# Revit family: 13323XXX
name_source: partatom
category: Plumbing Fixtures
units: mm (PartAtom-declared; Revit-internal decimal feet)

## family parameters
Always vertical = No
Cut with Voids When Loaded = No
OmniClass Number = 23.31.17.00
OmniClass Title = Showers
Part Type = Normal
Room Calculation Point = No
Round Connector Dimension = Use Diameter
Shared = No
Work Plane-Based = Yes

## types (1)
- 000 Chrome
    Connector Description = Water Inlet 12.7mm
    Default Elevation = 1219 mm
    Description = Ecostat Fine Shower thermostat for exposed installation with locked safety stop
    Diameter = 13 mm
    Manufacturer = Hansgrohe
    Material = Hansgrohe - Metal - 000 Chrome
    Model = 13323XXX
    Product Guid = b28cb2af-97a2-4dc1-9092-925d3b888c1d
    Product Page URL = https://www.hansgrohe.com
    Product data url = https://bimobject.com
    URL = https://www.hansgrohe.com
    Version = 1

## geometry (parser evidence)
native form markers: Sweep x3
no freeform markers — native parametric forms only
